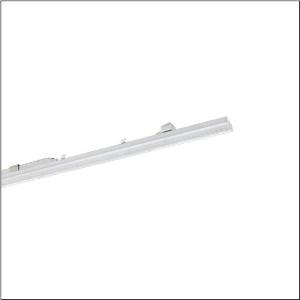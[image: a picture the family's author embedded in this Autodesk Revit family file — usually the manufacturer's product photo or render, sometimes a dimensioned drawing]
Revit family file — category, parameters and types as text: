
# Revit family: tl_l_5wd7a8f0b2b5
name_source: partatom
category: Lighting Fixtures
units: mm (PartAtom-declared; Revit-internal decimal feet)

## family parameters
Cut with Voids When Loaded = No
Host = Face
Light Source = No
Part Type = Normal
Room Calculation Point = No
Round Connector Dimension = Use Diameter
Shared = No

## types (1)
- TL L (1 x LED, 4990 lm, 30 W, 4000K)
    Apparent Load = 30 VA
    CIE Flux Codes = 49 84 98 100 100
    Color Rendering = 80
    Color Temperature = 4000K
    Default Elevation = 1800 mm
    Description = TL L, luminaire insert, of sheet steel, galvanised, coil coated, white, length: 1.500mm, width: 66mm, height: 67mm, micro fuse,LED rated luminous flux: 4.990lm, light colour: 840, control gear: 4..20mA, with terminal, 5-pole, mains connection: 230..240V, AC, 50/60Hz, rated input power: 30W, primary optical cover: cover, of PMMA, light emission: direct distribution, protection rating (complete): as luminaire, insulation class (complete): insulation class I (protective earthing), certification: CE, impact resistance: IK06, permissible ambient temperature for indoor applications: -25..+35°C, packaging unit: 1 piece
    Height = 120 mm
    Lamp = 1 x LED
    Lamp Light Flux = 4990 lm
    Lamp Power = 30 W
    Lamp count = 1
    Length = 1690 mm
    Luminous efficacy = 166 lm/W
    Manufacturer = Siteco
    ModVariant = No
    Model = 5WD7A8F0B2B5
    Mounting Place = Ceiling
    Mounting Type = Pendant
    Number of Poles = 1
    OnlyDefault = Yes
    Power Factor = 1
    Product Name = TL L
    Product group = luminaire insert
    ProductGroupID = 901
    Protection Class = Protection class I
    Protection Degree = Degree of protection
    RLX_Detail_Level = 1
    RLX_Emergency_Light_Flux = 0 lm
    RLX_Emergency_Type = 0
    RLX_Emergency_Type_DB = No
    RlxData = <blob elided: 14121 chars, md5=b391b777>
    Socket = socket
    Standby Power = 0 W
    System Light Flux = 4990 lm
    System Power = 30 W
    Type Comments = Product without accessories
    Type Image = l_1294382.jpg
    URL = http://relux.com
    VarID = ---
    Voltage = 0 V
    Weight = 0.00 kg
    Width = 208 mm

## geometry (parser evidence)
native form markers: Sweep x12
no freeform markers — native parametric forms only
